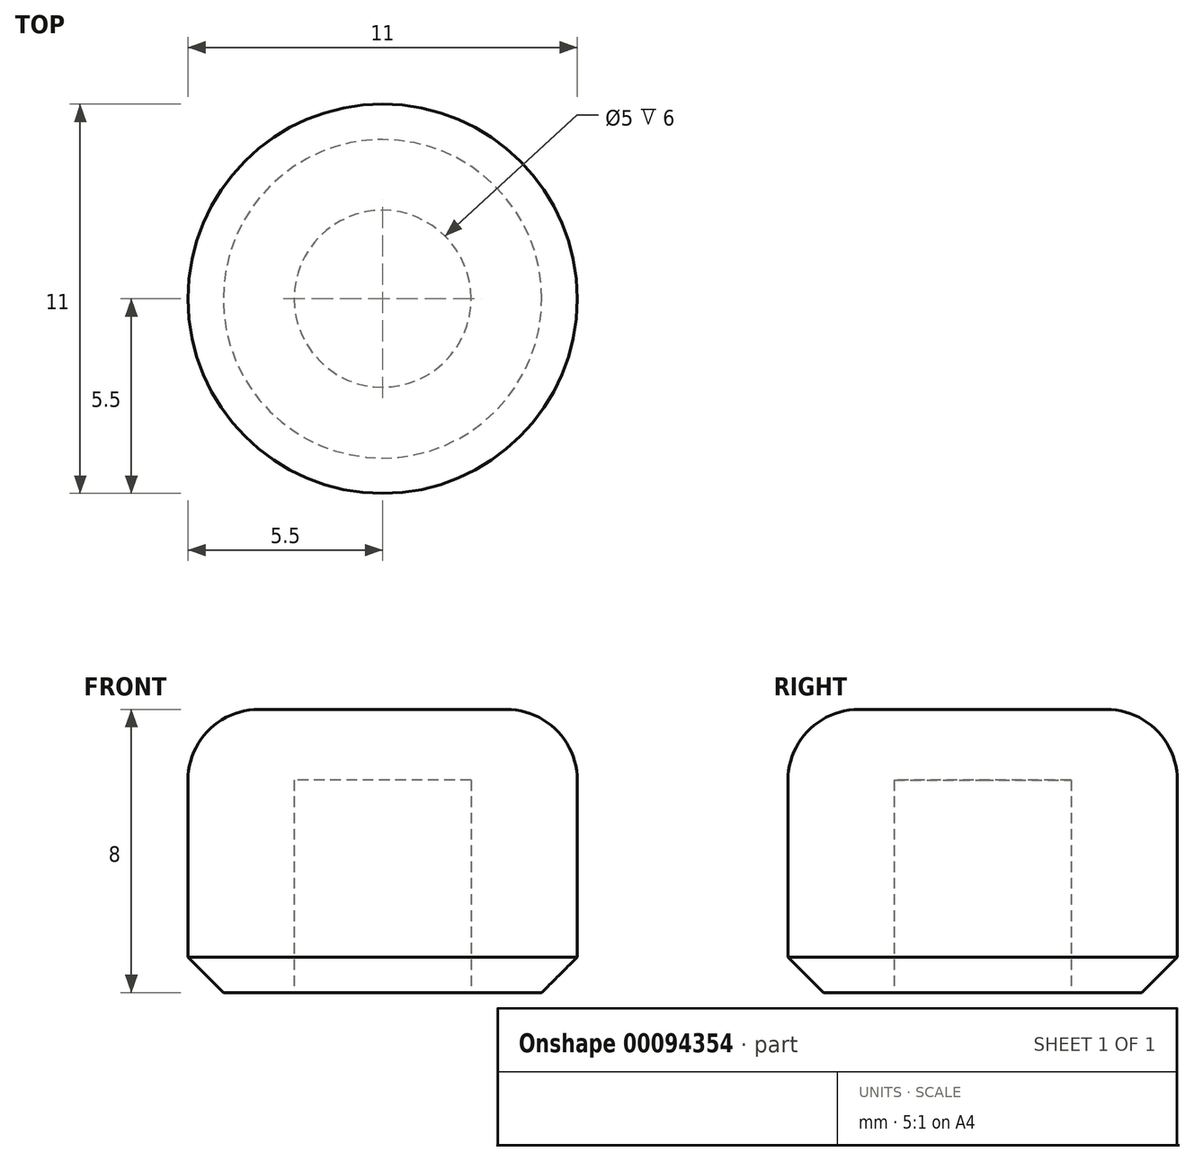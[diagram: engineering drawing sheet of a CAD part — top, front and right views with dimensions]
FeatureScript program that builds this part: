
annotation { "Feature Type Name" : "Feature", "Feature Type Description" : "" }
export const myFeature = defineFeature(function(context is Context, id is Id, definition is map)
    precondition{}
    {
        {
            var Q0;
            Q0=qCreatedBy(makeId("Top.planeOp"),FACE);
            var sketch = newSketch(context, id + "F0", { "sketchPlane" : qUnion([Q0])});
            skCircle(sketch, "E0", {"center": v(0, 0) * mm, "radius": 5.5 * mm});
            skCircle(sketch, "E1", {"center": v(0, 0) * mm, "radius": 2.5 * mm});
            skSolve(sketch);
        }
        {
            var Q0;
            Q0=makeQuery(id+"F0.imprint","IMPRINT",FACE,{"disambiguationData":[TD([[makeQuery(id+"F0.imprint","IMPRINT",EDGE,{"derivedFrom":sQuery(id+"F0.wireOp",EDGE,"E0")}),1.0]])]});
            var Q1;
            Q1=makeQuery(id+"F0.imprint","IMPRINT",FACE,{"disambiguationData":[TD([[makeQuery(id+"F0.imprint","IMPRINT",EDGE,{"derivedFrom":sQuery(id+"F0.wireOp",EDGE,"E1")}),1.0]])]});
            extrude(context, id + "F1", {"entities" : qUnion([Q0, Q1]), "depth" : 8 * mm});
        }
        {
            var Q0;
            Q0=makeQuery(id+"F1.opExtrude","CAP_EDGE",EDGE,{"disambiguationData":[OSD([sQuery(id+"F0.wireOp",EDGE,"E0")])],"isStart":false});
            fillet(context, id + "F2", {"entities" : qUnion([Q0]), "radius" : 2 * mm, "tangentPropagation" : true, "allowEdgeOverflow" : false});
        }
        {
            var Q0;
            Q0=makeQuery(id+"F0.imprint","IMPRINT",FACE,{"disambiguationData":[TD([[makeQuery(id+"F0.imprint","IMPRINT",EDGE,{"derivedFrom":sQuery(id+"F0.wireOp",EDGE,"E1")}),1.0]])]});
            extrude(context, id + "F3", {"entities" : qUnion([Q0]), "operationType" : NewBodyOperationType.REMOVE, "depth" : 6 * mm});
        }
        {
            var Q0;
            Q0=makeQuery(id+"F1.opExtrude","CAP_EDGE",EDGE,{"disambiguationData":[OSD([sQuery(id+"F0.wireOp",EDGE,"E0")])],"isStart":true});
            chamfer(context, id + "F4", {"entities" : qUnion([Q0]), "width" : 1 * mm, "tangentPropagation" : true});
        }
    });
